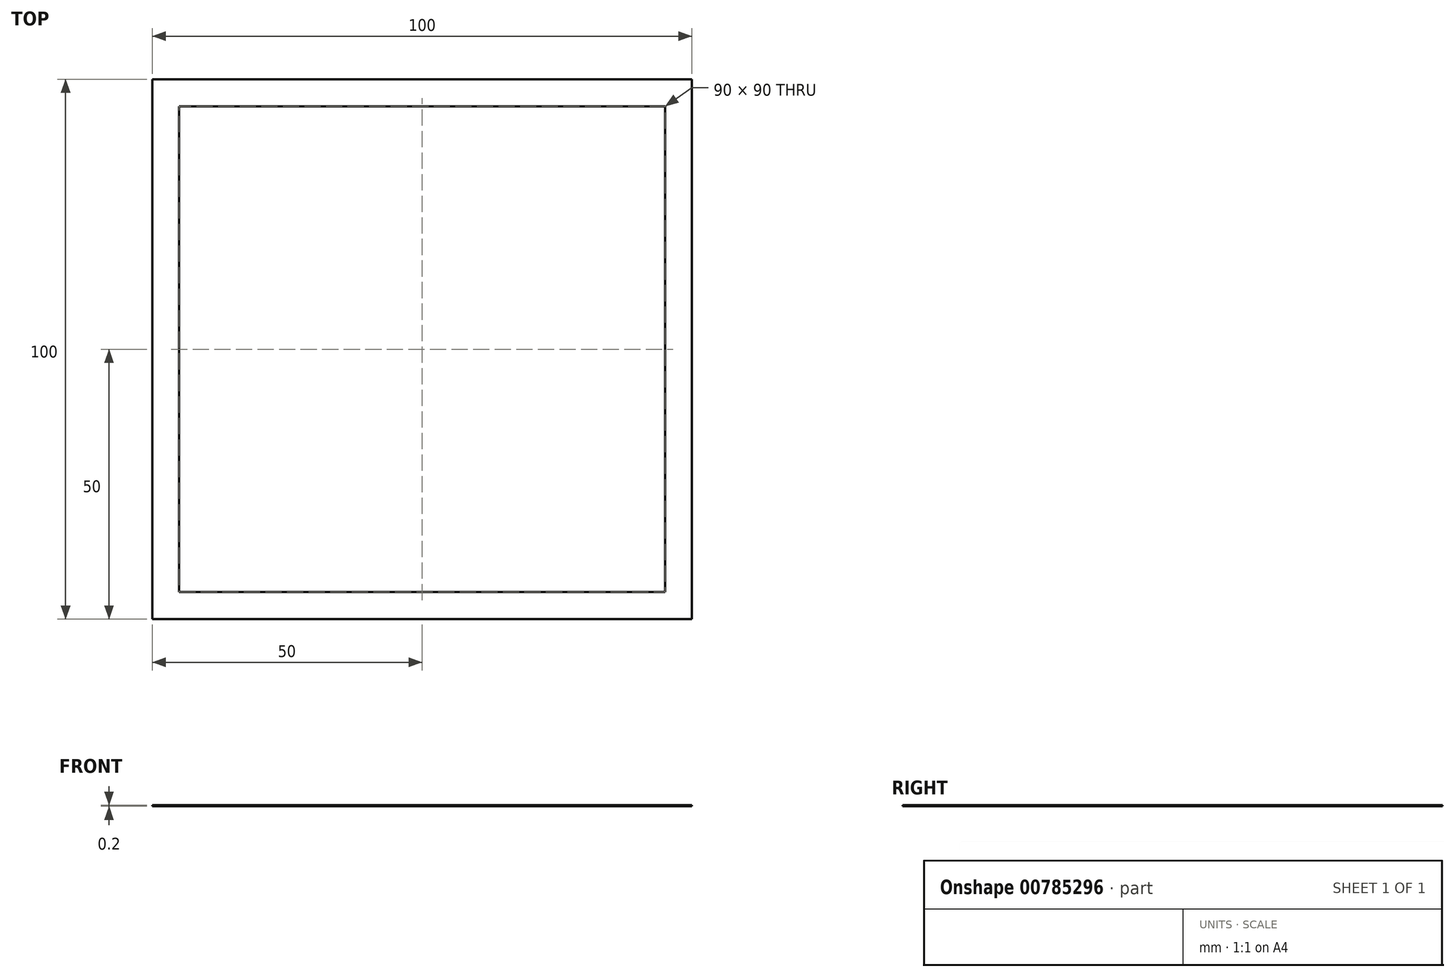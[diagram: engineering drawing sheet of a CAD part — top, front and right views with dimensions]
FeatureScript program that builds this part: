
annotation { "Feature Type Name" : "Feature", "Feature Type Description" : "" }
export const myFeature = defineFeature(function(context is Context, id is Id, definition is map)
    precondition{}
    {
        {
            var Q0;
            Q0=qCreatedBy(makeId("Top.planeOp"),FACE);
            var sketch = newSketch(context, id + "F0", { "sketchPlane" : qUnion([Q0])});
            skLineSegment(sketch, "E0.bottom", {"start": v(50, -50) * mm, "end": v(-50, -50) * mm});
            skLineSegment(sketch, "E0.top", {"start": v(50, 50) * mm, "end": v(-50, 50) * mm});
            skLineSegment(sketch, "E0.left", {"start": v(50, -50) * mm, "end": v(50, 50) * mm});
            skLineSegment(sketch, "E0.right", {"start": v(-50, -50) * mm, "end": v(-50, 50) * mm});
            skPoint(sketch, "E0.middle", {"position": v(0, 0) * mm});
            skLineSegment(sketch, "E1.0", {"start": v(-45, -45) * mm, "end": v(-45, 45) * mm});
            skLineSegment(sketch, "E1.1", {"start": v(45, -45) * mm, "end": v(-45, -45) * mm});
            skLineSegment(sketch, "E1.2", {"start": v(45, -45) * mm, "end": v(45, 45) * mm});
            skLineSegment(sketch, "E1.3", {"start": v(45, 45) * mm, "end": v(-45, 45) * mm});
            skSolve(sketch);
        }
        {
            var Q0;
            Q0=makeQuery(id+"F0.imprint","IMPRINT",FACE,{"disambiguationData":[TD([[makeQuery(id+"F0.imprint","IMPRINT",EDGE,{"derivedFrom":sQuery(id+"F0.wireOp",EDGE,"E0.bottom")}),-1.0]])]});
            extrude(context, id + "F1", {"entities" : qUnion([Q0]), "depth" : 0.2 * mm, "offsetDistance" : 25 * mm});
        }
    });
